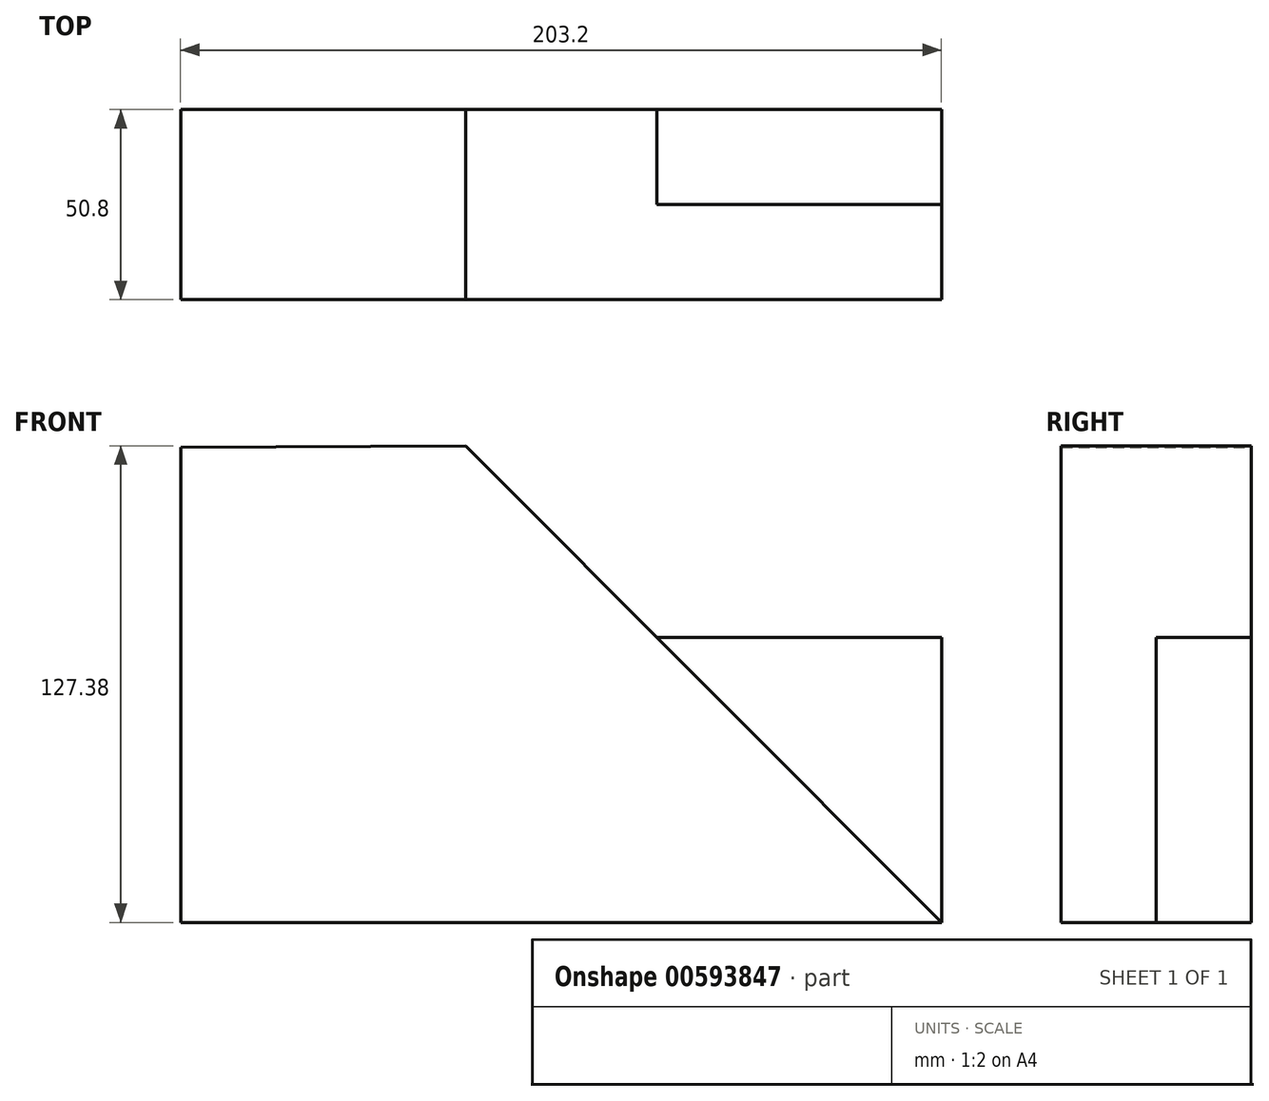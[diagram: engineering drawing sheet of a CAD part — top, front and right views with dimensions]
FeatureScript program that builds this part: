
annotation { "Feature Type Name" : "Feature", "Feature Type Description" : "" }
export const myFeature = defineFeature(function(context is Context, id is Id, definition is map)
    precondition{}
    {
        {
            var Q0;
            Q0=qCreatedBy(makeId("Front.planeOp"),FACE);
            var sketch = newSketch(context, id + "F0", { "sketchPlane" : qUnion([Q0])});
            skLineSegment(sketch, "E0", {"start": v(-99.63, 72.07) * mm, "end": v(-99.63, -54.93) * mm});
            skLineSegment(sketch, "E1", {"start": v(-99.63, -54.93) * mm, "end": v(103.57, -54.93) * mm});
            skLineSegment(sketch, "E2", {"start": v(103.57, -54.93) * mm, "end": v(103.57, 73.08) * mm});
            skLineSegment(sketch, "E3", {"start": v(103.57, 73.08) * mm, "end": v(-99.63, 72.07) * mm});
            skLineSegment(sketch, "E4", {"start": v(-23.43, 72.45) * mm, "end": v(103.57, -54.93) * mm});
            skPoint(sketch, "E5.startSnap0", {"position": v(40.07, 8.76) * mm});
            skPoint(sketch, "E5.endSnap0", {"position": v(103.57, 9.07) * mm});
            skPoint(sketch, "E5.endSnap1", {"position": v(40.07, 8.76) * mm});
            skLineSegment(sketch, "E6", {"start": v(27.6, 21.27) * mm, "end": v(103.57, 21.27) * mm});
            skSolve(sketch);
        }
        {
            var Q0;
            {var subQ5=sQuery(id+"F0.wireOp",EDGE,"E0");Q0=makeQuery(id+"F0.imprint","IMPRINT",FACE,{"disambiguationData":[TD([[makeQuery(id+"F0.imprint","IMPRINT",EDGE,{"derivedFrom":subQ5}),1.0]])]});}
            extrude(context, id + "F1", {"entities" : qUnion([Q0]), "endBound" : BoundingType.SYMMETRIC, "depth" : 50.8 * mm, "offsetDistance" : 25.4 * mm});
        }
        {
            var Q0;
            {var subQ3=sQuery(id+"F0.wireOp",EDGE,"E6");Q0=makeQuery(id+"F0.imprint","IMPRINT",FACE,{"disambiguationData":[TD([[makeQuery(id+"F0.imprint","IMPRINT",EDGE,{"derivedFrom":subQ3}),-1.0]])]});}
            extrude(context, id + "F2", {"entities" : qUnion([Q0]), "operationType" : NewBodyOperationType.ADD, "oppositeDirection" : true, "depth" : 25.4 * mm, "offsetDistance" : 25.4 * mm});
        }
    });
